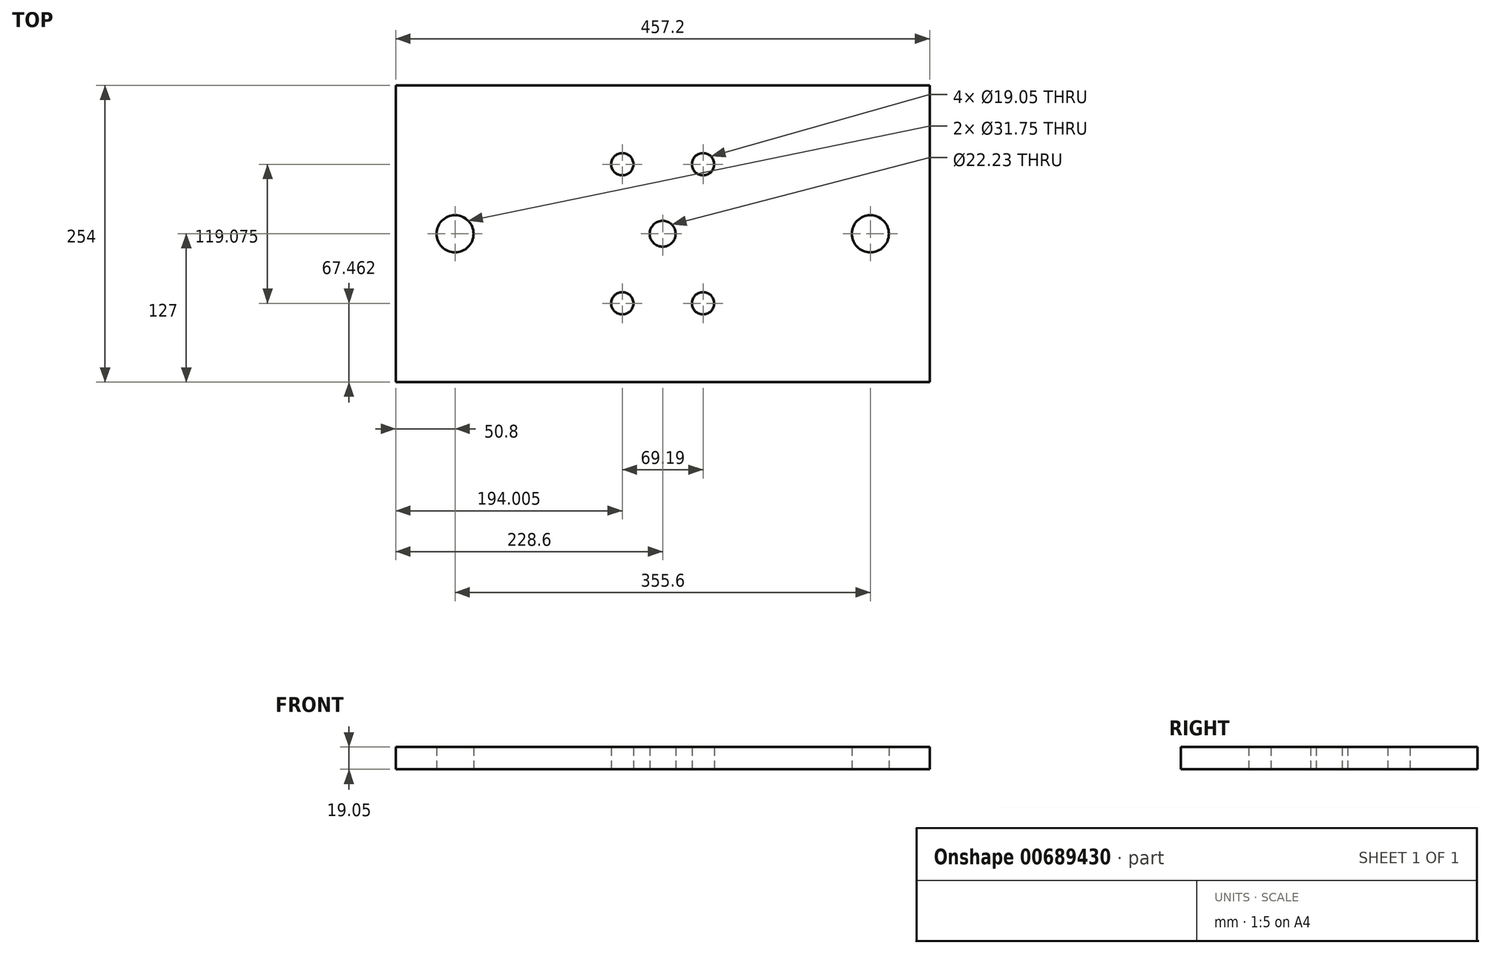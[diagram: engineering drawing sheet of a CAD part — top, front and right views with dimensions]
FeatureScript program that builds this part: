
annotation { "Feature Type Name" : "Feature", "Feature Type Description" : "" }
export const myFeature = defineFeature(function(context is Context, id is Id, definition is map)
    precondition{}
    {
        {
            var Q0;
            Q0=qCreatedBy(makeId("Top.planeOp"),FACE);
            var sketch = newSketch(context, id + "F0", { "sketchPlane" : qUnion([Q0])});
            skLineSegment(sketch, "E0.bottom", {"start": v(-228.6, 127) * mm, "end": v(228.6, 127) * mm});
            skLineSegment(sketch, "E0.top", {"start": v(-228.6, -127) * mm, "end": v(228.6, -127) * mm});
            skLineSegment(sketch, "E0.left", {"start": v(-228.6, 127) * mm, "end": v(-228.6, -127) * mm});
            skLineSegment(sketch, "E0.right", {"start": v(228.6, 127) * mm, "end": v(228.6, -127) * mm});
            skPoint(sketch, "E0.middle", {"position": v(0, 0) * mm});
            skCircle(sketch, "E1", {"center": v(-177.8, 0) * mm, "radius": 15.88 * mm});
            skCircle(sketch, "E2", {"center": v(177.8, 0) * mm, "radius": 15.88 * mm});
            skCircle(sketch, "E3", {"center": v(34.6, 59.54) * mm, "radius": 9.53 * mm});
            skCircle(sketch, "E4", {"center": v(-34.6, 59.54) * mm, "radius": 9.53 * mm});
            skCircle(sketch, "E5", {"center": v(34.6, -59.54) * mm, "radius": 9.53 * mm});
            skCircle(sketch, "E6", {"center": v(-34.6, -59.54) * mm, "radius": 9.53 * mm});
            skCircle(sketch, "E7", {"center": v(0, 0) * mm, "radius": 11.11 * mm});
            skSolve(sketch);
        }
        {
            var Q0;
            Q0=makeQuery(id+"F0.imprint","IMPRINT",FACE,{"disambiguationData":[TD([[makeQuery(id+"F0.imprint","IMPRINT",EDGE,{"derivedFrom":sQuery(id+"F0.wireOp",EDGE,"E0.bottom")}),-1.0]])]});
            extrude(context, id + "F1", {"entities" : qUnion([Q0]), "depth" : 19.05 * mm, "offsetDistance" : 25.4 * mm});
        }
    });
